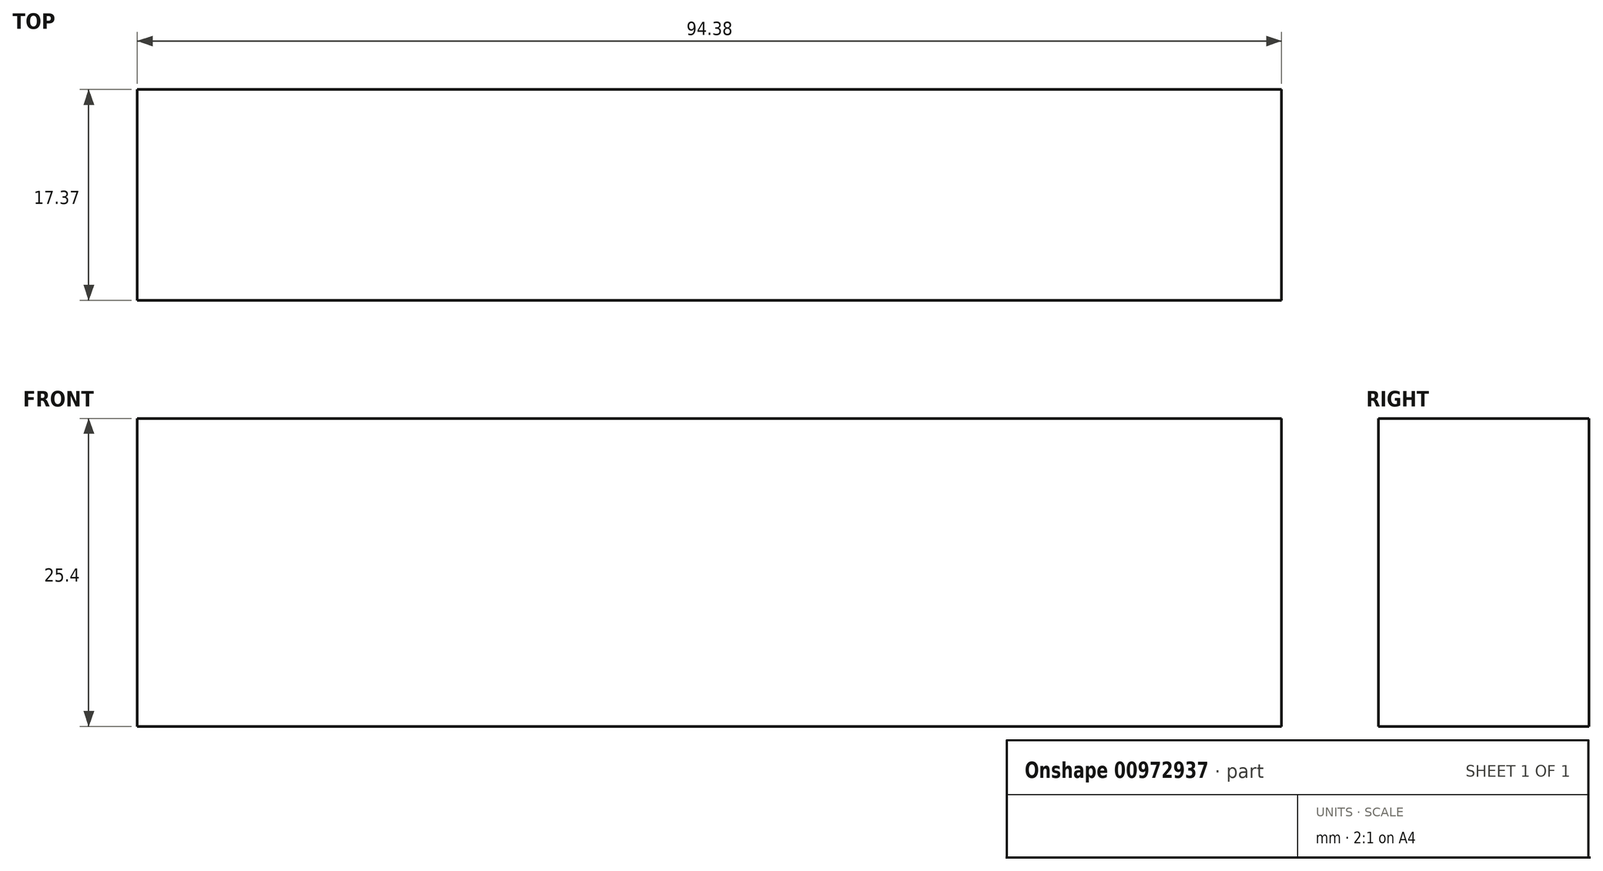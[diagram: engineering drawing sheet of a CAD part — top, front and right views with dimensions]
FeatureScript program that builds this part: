
annotation { "Feature Type Name" : "Feature", "Feature Type Description" : "" }
export const myFeature = defineFeature(function(context is Context, id is Id, definition is map)
    precondition{}
    {
        {
            var Q0;
            Q0=qCreatedBy(makeId("Top.planeOp"),FACE);
            var sketch = newSketch(context, id + "F0", { "sketchPlane" : qUnion([Q0])});
            skLineSegment(sketch, "E0.bottom", {"start": v(-55.4, -10.74) * mm, "end": v(38.98, -10.74) * mm});
            skLineSegment(sketch, "E0.top", {"start": v(-55.4, 6.63) * mm, "end": v(38.98, 6.63) * mm});
            skLineSegment(sketch, "E0.left", {"start": v(-55.4, -10.74) * mm, "end": v(-55.4, 6.63) * mm});
            skLineSegment(sketch, "E0.right", {"start": v(38.98, -10.74) * mm, "end": v(38.98, 6.63) * mm});
            skSolve(sketch);
        }
        {
            var Q0;
            Q0 = qSketchRegion(id + "F0", true);
            extrude(context, id + "F1", {"entities" : qUnion([Q0]), "depth" : 25.4 * mm, "offsetDistance" : 25.4 * mm});
        }
    });
